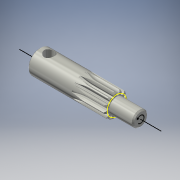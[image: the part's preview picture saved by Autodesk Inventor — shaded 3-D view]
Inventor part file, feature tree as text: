
AUTODESK INVENTOR PART (.ipt)
format: ipt  version: 2017 (Build 210142000, 142)  size: 914,944 bytes
history: native  units: mm (DEFAULTED — no unit token found)
features: sketch x21, projected_geometry x17, revolve x12, extrude x4, plane x3, other x2, chamfer x2, pattern_circular x1, hole x1
ambient origin geometry x5: Origin, X Axis, Y Axis, Z Axis, Center Point
bodies: Solid1 (feature_tree)
feature tree (63):
  other  "Embedding 1"
  extrude  "Extrusion1"  Depth=2.116667mm
  pattern_circular  "Circular Pattern1"  Count=12  [1 undecoded]
  extrude  "Extrusion2"  Depth=29.758mm
  extrude  "Extrusion3"  Depth=18.9992mm
  chamfer  "Chamfer1"  Distance=30.1498mm
  chamfer  "Chamfer2"  Distance=1.5875mm
  plane  "Work Plane2"
  extrude  "Extrusion4"  Depth=16.75mm
  plane  "Work Plane3"
  revolve  "Revolution1"  [1 undecoded]
  revolve  "Revolution2"  [1 undecoded]
  revolve  "Revolution3"  [1 undecoded]
  sketch  "Sketch13"  dims[d8=0.498475mm]
  revolve  "Revolution5"  [1 undecoded]
  revolve  "Revolution6"  [1 undecoded]
  revolve  "Revolution7"  Angle=90.0deg
  revolve  "Revolution8"  [1 undecoded]
  revolve  "Revolution9"  Angle=90.0deg
  revolve  "Revolution10"  Angle=90.0deg
  revolve  "Revolution11"  [1 undecoded]
  revolve  "Revolution12"  [1 undecoded]
  revolve  "Revolution13"  Angle=90.0deg
  hole  "Hole1"  [1 undecoded]
  sketch  "Sketch24"  dims[d40=40.0mm d42=90.0deg]
  other  "Work Axis2"
  sketch  "Sketch25"  dims[d43=90.0deg d44=40.0mm]
  plane  "Work Plane4"
  sketch  "Sketch26"  dims[d45=90.0deg d48=90.0deg]
  sketch  "Sketch27"  dims[d49=40.0mm d50=90.0deg d51=40.0mm d52=40.0mm d53=90.0deg d54=40.0mm d55=90.0deg d56=40.0mm d57=90.0deg d58=40.0mm d59=90.0deg d60=4.978mm d61=6.0mm d62=4.0mm d63=2.0mm d64=14.3117mm d65=8.0mm d66=20.594885mm d67=45.0deg d68=45.0deg d69=29.758mm]
  sketch  "Sketch1"  dims[d0=25.4mm d1=2.116667mm]
  sketch  "Sketch2"  dims[d2=3.490659mm]
  sketch  "Sketch3"  dims[d3=4.56565mm]
  sketch  "Sketch4"  dims[d4=6.7945mm]
  sketch  "Sketch10"  dims[d5=5.545667mm]
  projected_geometry  "Projected Loop2"
  projected_geometry  "Projected Loop3"
  projected_geometry  "Projected Loop4"
  projected_geometry  "Projected Loop5"
  sketch  "Sketch11"  dims[d6=1.308997mm]
  projected_geometry  "Projected Loop6"
  sketch  "Sketch12"  dims[d7=1.308997mm]
  projected_geometry  "Projected Loop7"
  projected_geometry  "Projected Loop8"
  sketch  "Sketch14"  dims[d9=25.4mm d10=0.0mm d11=120.0mm]
  projected_geometry  "Projected Loop9"
  sketch  "Sketch15"  dims[d13=360.0deg d14=29.758mm]
  projected_geometry  "Projected Loop10"
  sketch  "Sketch16"  dims[d15=71.4502mm d16=0.0mm d17=18.9992mm d18=30.1498mm d19=0.0mm d20=1.5875mm d21=2.0mm]
  projected_geometry  "Projected Loop11"
  sketch  "Sketch17"  dims[d22=1.5875mm d23=2.0mm d25=16.75mm]
  projected_geometry  "Projected Loop12"
  sketch  "Sketch18"  dims[d26=13.081mm d27=12.7mm]
  projected_geometry  "Projected Loop13"
  sketch  "Sketch19"  dims[d28=50.8mm d29=0.0mm d32=40.0mm]
  projected_geometry  "Projected Loop14"
  sketch  "Sketch20"  dims[d33=90.0deg d35=40.0mm]
  projected_geometry  "Projected Loop15"
  sketch  "Sketch21"  dims[d36=90.0deg d37=40.0mm]
  projected_geometry  "Projected Loop16"
  sketch  "Sketch22"  dims[d38=90.0deg d39=40.0mm]
  projected_geometry  "Projected Loop17"
  projected_geometry  "Project Cut Edges2"
note: 10 required parameter values undecoded (feature->parameter linkage not recoverable at this tier; creation-order binding heuristic only, values carry confidence <= 0.55)